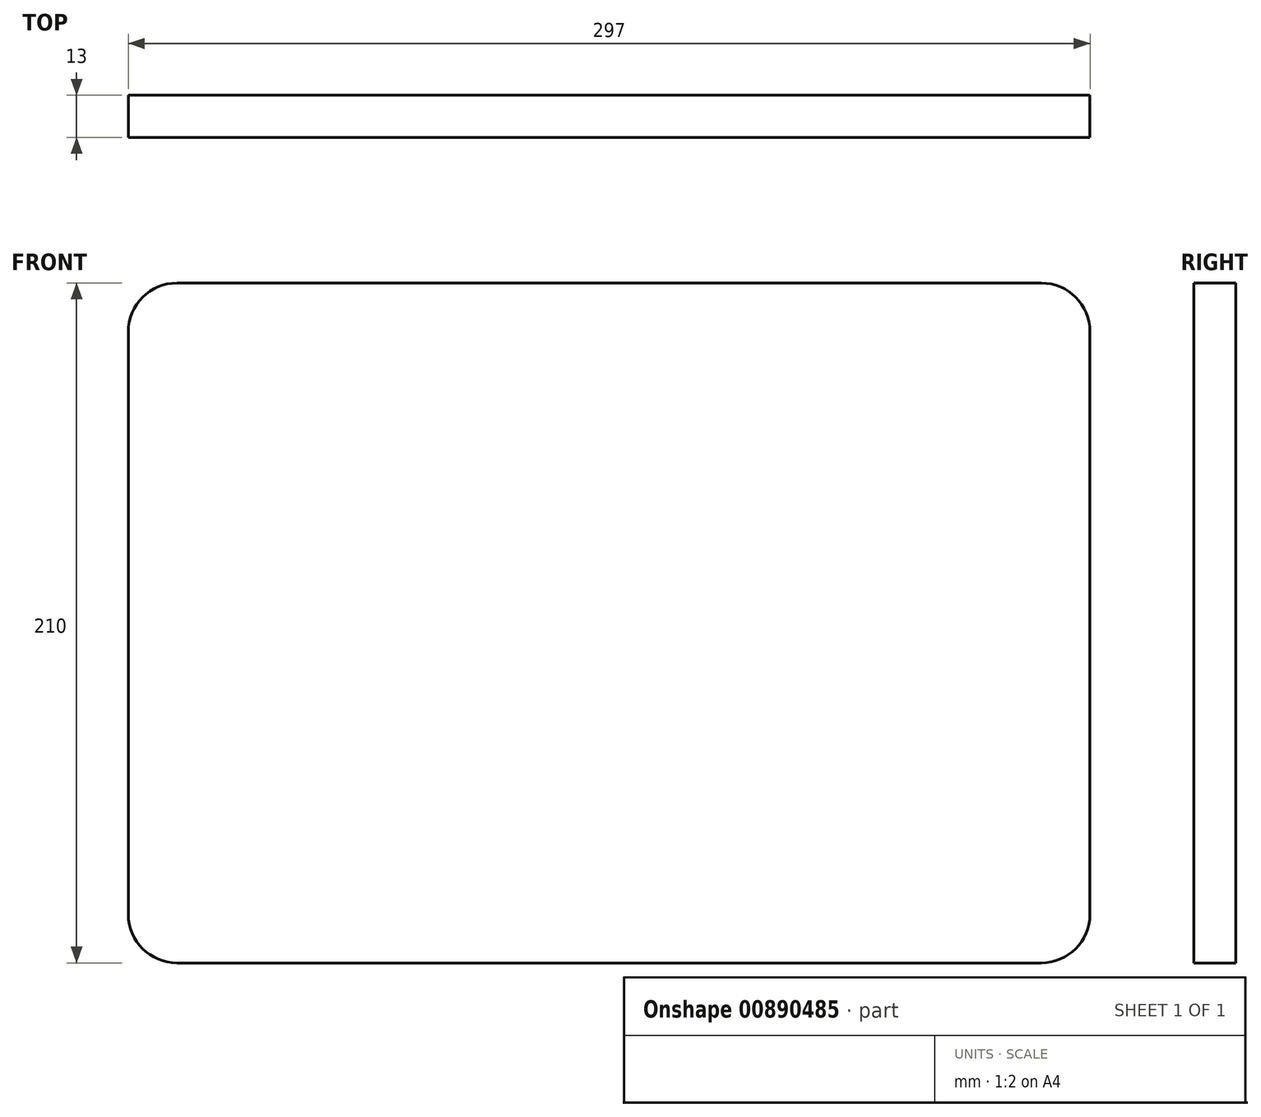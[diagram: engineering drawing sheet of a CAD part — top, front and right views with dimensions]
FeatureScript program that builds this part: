
annotation { "Feature Type Name" : "Feature", "Feature Type Description" : "" }
export const myFeature = defineFeature(function(context is Context, id is Id, definition is map)
    precondition{}
    {
        {
            var Q0;
            Q0=qCreatedBy(makeId("Front.planeOp"),FACE);
            var sketch = newSketch(context, id + "F0", { "sketchPlane" : qUnion([Q0])});
            skLineSegment(sketch, "E0.bottom", {"start": v(-134.7, 96.04) * mm, "end": v(132.3, 96.04) * mm});
            skLineSegment(sketch, "E0.top", {"start": v(-134.7, -113.96) * mm, "end": v(132.3, -113.96) * mm});
            skLineSegment(sketch, "E0.left", {"start": v(-149.7, 81.04) * mm, "end": v(-149.7, -98.96) * mm});
            skLineSegment(sketch, "E0.right", {"start": v(147.3, 81.04) * mm, "end": v(147.3, -98.96) * mm});
            skPoint(sketch, "E1.visualSharp", {"position": v(-149.7, 96.04) * mm});
            skArc(sketch, "E1.filletArc", {"start": v(-134.7, 96.04) * mm, "mid": v(-145.31, 91.65) * mm, "end": v(-149.7, 81.04) * mm});
            skPoint(sketch, "E2.visualSharp", {"position": v(147.3, 96.04) * mm});
            skArc(sketch, "E2.filletArc", {"start": v(147.3, 81.04) * mm, "mid": v(142.9, 91.65) * mm, "end": v(132.3, 96.04) * mm});
            skPoint(sketch, "E3.visualSharp", {"position": v(147.3, -113.96) * mm});
            skArc(sketch, "E3.filletArc", {"start": v(132.3, -113.96) * mm, "mid": v(142.9, -109.57) * mm, "end": v(147.3, -98.96) * mm});
            skPoint(sketch, "E4.visualSharp", {"position": v(-149.7, -113.96) * mm});
            skArc(sketch, "E4.filletArc", {"start": v(-149.7, -98.96) * mm, "mid": v(-145.31, -109.57) * mm, "end": v(-134.7, -113.96) * mm});
            skSolve(sketch);
        }
        {
            var Q0;
            Q0 = qSketchRegion(id + "F0", true);
            extrude(context, id + "F1", {"entities" : qUnion([Q0]), "depth" : 13 * mm, "offsetDistance" : 25 * mm});
        }
        {
            var Q0;
            Q0=makeQuery(id+"F1.opExtrude","CAP_FACE",FACE,{"disambiguationData":[OSD([sQuery(id+"F0.wireOp",EDGE,"E0.bottom"),sQuery(id+"F0.wireOp",EDGE,"E0.top"),sQuery(id+"F0.wireOp",EDGE,"E0.left"),sQuery(id+"F0.wireOp",EDGE,"E0.right"),sQuery(id+"F0.wireOp",EDGE,"E1.filletArc"),sQuery(id+"F0.wireOp",EDGE,"E2.filletArc"),sQuery(id+"F0.wireOp",EDGE,"E3.filletArc"),sQuery(id+"F0.wireOp",EDGE,"E4.filletArc")])],"isStart":false});
            var sketch = newSketch(context, id + "F2", { "sketchPlane" : qUnion([Q0])});
            skLineSegment(sketch, "E5.bottom", {"start": v(147.3, -54.29) * mm, "end": v(19.22, -54.29) * mm});
            skLineSegment(sketch, "E5.top", {"start": v(147.3, -80.86) * mm, "end": v(19.22, -80.86) * mm});
            skLineSegment(sketch, "E5.left", {"start": v(147.3, -54.29) * mm, "end": v(147.3, -80.86) * mm});
            skLineSegment(sketch, "E5.right", {"start": v(19.22, -54.29) * mm, "end": v(19.22, -80.86) * mm});
            skSolve(sketch);
        }
        {
            var Q0;
            Q0=sQuery(id+"F2.wireOp",EDGE,"E5.bottom");
            extrude(context, id + "F3", {"bodyType" : ToolBodyType.SURFACE, "surfaceEntities" : qUnion([Q0]), "depth" : 25 * mm, "offsetDistance" : 25 * mm});
        }
    });
